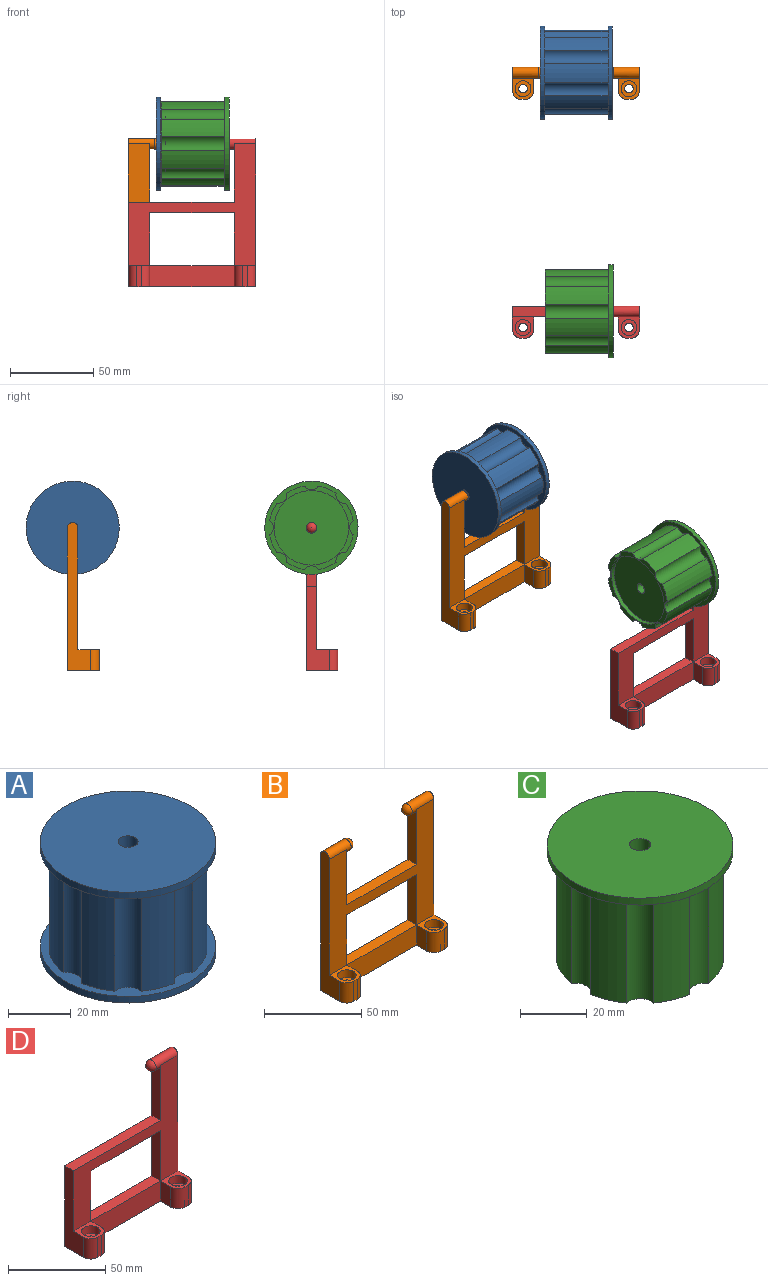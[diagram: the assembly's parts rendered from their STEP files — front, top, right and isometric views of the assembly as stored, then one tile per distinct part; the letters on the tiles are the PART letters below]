
ASSEMBLY  parts=4 mates=4
PART A: 23 faces, bbox 55.9x55.9x43.2 mm
  f0: cylinder r=25.4mm len=38.1mm, axis (0,0,-1), area 440.1mm2, adj f10,f11,f18,f21
  f1: cylinder r=25.4mm len=38.1mm, axis (0,0,-1), area 440.1mm2, adj f10,f17,f18,f21
  f2: cylinder r=25.4mm len=38.1mm, axis (0,0,-1), area 440.1mm2, adj f10,f16,f17,f21
  f3: cylinder r=25.4mm len=38.1mm, axis (0,0,-1), area 440.1mm2, adj f10,f15,f16,f21
  f4: cylinder r=25.4mm len=38.1mm, axis (0,0,-1), area 440.1mm2, adj f10,f14,f15,f21
  f5: cylinder r=25.4mm len=38.1mm, axis (0,0,-1), area 440.1mm2, adj f10,f13,f14,f21
  f6: cylinder r=25.4mm len=38.1mm, axis (0,0,-1), area 440.1mm2, adj f10,f12,f13,f21
  f7: cylinder r=25.4mm len=38.1mm, axis (0,0,-1), area 440.1mm2, adj f10,f11,f12,f21
  f8: cylinder r=27.94mm len=55.88mm, axis (0,0,-1), area 445.9mm2, adj f9,f10
  f9: plane 55.88x55.88mm, normal (0,0,1), area 2420.8mm2, adj f8,f22
  f10: plane 55.88x55.88mm, normal (0,0,-1), area 544.1mm2, adj f0,f1,f2,f3,f4,f5,f6,f7
  f11: cylinder r=5.08mm len=38.1mm, axis (0,0,-1), area 374.1mm2, adj f0,f7,f10,f21
  f12: cylinder r=5.08mm len=38.1mm, axis (0,0,-1), area 374.1mm2, adj f6,f7,f10,f21
  f13: cylinder r=5.08mm len=38.1mm, axis (0,0,-1), area 374.1mm2, adj f5,f6,f10,f21
  f14: cylinder r=5.08mm len=38.1mm, axis (0,0,-1), area 374.1mm2, adj f4,f5,f10,f21
  f15: cylinder r=5.08mm len=38.1mm, axis (0,0,-1), area 374.1mm2, adj f3,f4,f10,f21
  f16: cylinder r=5.08mm len=38.1mm, axis (0,0,-1), area 374.1mm2, adj f2,f3,f10,f21
  f17: cylinder r=5.08mm len=38.1mm, axis (0,0,-1), area 374.1mm2, adj f1,f2,f10,f21
  f18: cylinder r=5.08mm len=38.1mm, axis (0,0,-1), area 374.1mm2, adj f0,f1,f10,f21
  f19: cylinder r=27.94mm len=55.88mm, axis (0,0,1), area 445.9mm2, adj f20,f21
  f20: plane 55.88x55.88mm, normal (0,0,-1), area 2420.8mm2, adj f19,f22
  f21: plane 55.88x55.88mm, normal (0,0,1), area 544.1mm2, adj f0,f1,f2,f3,f4,f5,f6,f7
  f22: cylinder r=3.17mm len=43.18mm, axis (0,0,-1), area 861.4mm2, adj f9,f20
PART B: 33 faces, bbox 76.2x19.1x88.9 mm
  f0: plane 50.8x12.7mm, normal (0,-1,0), area 645.2mm2, adj f3,f16,f17,f20
  f1: plane 76.2x73.03mm, normal (0,-1,0), area 2177.4mm2, adj f4,f5,f6,f7,f8,f9,f10,f13
  f2: plane 85.73x76.2mm, normal (0,1,0), area 3145.2mm2, adj f3,f4,f5,f6,f7,f8,f9,f10
  f3: plane 76.2x19.05mm, normal (0,0,-1), area 743.4mm2, adj f0,f2,f4,f5,f17,f19,f20,f22
  f4: plane 88.9x13.97mm, normal (1,0,0), area 657mm2, adj f1,f2,f3,f10,f21,f29
  f5: plane 88.9x13.97mm, normal (-1,0,0), area 657mm2, adj f1,f2,f3,f9,f18,f32
  f6: plane 34.93x6.35mm, normal (-1,0,0), area 205.9mm2, adj f1,f2,f8,f10
  f7: plane 34.93x6.35mm, normal (1,0,0), area 205.9mm2, adj f1,f2,f8,f9
  f8: plane 50.8x6.35mm, normal (0,0,1), area 322.6mm2, adj f1,f2,f6,f7
  f9: cylinder r=3.17mm len=15.88mm, axis (-1,0,0), area 190mm2, adj f1,f2,f5,f7,f12
  f10: cylinder r=3.17mm len=15.88mm, axis (1,0,0), area 190mm2, adj f1,f2,f4,f6,f11
  f11: sphere r=3.17mm, area 63.3mm2, adj f10
  f12: sphere r=3.17mm, area 63.3mm2, adj f9
  f13: plane 31.75x6.35mm, normal (-1,0,0), area 201.6mm2, adj f1,f2,f14,f16
  f14: plane 50.8x6.35mm, normal (0,0,-1), area 322.6mm2, adj f1,f2,f13,f15
  f15: plane 31.75x6.35mm, normal (1,0,0), area 201.6mm2, adj f1,f2,f14,f16
  f16: plane 50.8x6.35mm, normal (0,0,1), area 322.6mm2, adj f0,f2,f13,f15
  f17: plane 12.7x7.62mm, normal (1,0,0), area 96.8mm2, adj f0,f3,f18,f31
  f18: plane 12.7x12.7mm, normal (0,0,1), area 79mm2, adj f1,f5,f17,f19,f25,f31,f32
  f19: plane 12.7x2.54mm, normal (0,-1,0), area 32.3mm2, adj f3,f18,f31,f32
  f20: plane 12.7x7.62mm, normal (-1,0,0), area 96.8mm2, adj f0,f3,f21,f30
  f21: plane 12.7x12.7mm, normal (0,0,1), area 79mm2, adj f1,f4,f20,f22,f28,f29,f30
  f22: plane 12.7x2.54mm, normal (0,-1,0), area 32.3mm2, adj f3,f21,f29,f30
  f23: cylinder r=2.55mm len=7.87mm, axis (0,0,1), area 126.3mm2, adj f3,f24
  f24: plane 9.53x9.53mm, normal (0,0,1), area 50.8mm2, adj f23,f25
  f25: cylinder r=4.76mm len=9.53mm, axis (0,0,1), area 144.4mm2, adj f18,f24
  f26: cylinder r=2.55mm len=7.87mm, axis (0,0,1), area 126.3mm2, adj f3,f27
  f27: plane 9.53x9.53mm, normal (0,0,1), area 50.8mm2, adj f26,f28
  f28: cylinder r=4.76mm len=9.53mm, axis (0,0,1), area 144.4mm2, adj f21,f27
  f29: cylinder r=5.08mm len=12.7mm, axis (0,0,-1), area 101.3mm2, adj f3,f4,f21,f22
  f30: cylinder r=5.08mm len=12.7mm, axis (0,0,1), area 101.3mm2, adj f3,f20,f21,f22
  f31: cylinder r=5.08mm len=12.7mm, axis (0,0,-1), area 101.3mm2, adj f3,f17,f18,f19
  f32: cylinder r=5.08mm len=12.7mm, axis (0,0,1), area 101.3mm2, adj f3,f5,f18,f19
PART C: 23 faces, bbox 55.9x55.9x40.6 mm
  f0: cylinder r=25.4mm len=38.1mm, axis (0,0,-1), area 440.1mm2, adj f1,f11,f15,f22
  f1: plane 50.11x50.11mm, normal (0,0,-1), area 338.8mm2, adj f0,f2,f3,f4,f5,f6,f7,f8
  f2: cylinder r=25.4mm len=38.1mm, axis (0,0,-1), area 440.1mm2, adj f1,f11,f21,f22
  f3: cylinder r=25.4mm len=38.1mm, axis (0,0,-1), area 440.1mm2, adj f1,f11,f20,f21
  f4: cylinder r=25.4mm len=38.1mm, axis (0,0,-1), area 440.1mm2, adj f1,f11,f19,f20
  f5: cylinder r=25.4mm len=38.1mm, axis (0,0,-1), area 440.1mm2, adj f1,f11,f18,f19
  f6: cylinder r=25.4mm len=38.1mm, axis (0,0,-1), area 440.1mm2, adj f1,f11,f17,f18
  f7: cylinder r=25.4mm len=38.1mm, axis (0,0,-1), area 440.1mm2, adj f1,f11,f16,f17
  f8: cylinder r=25.4mm len=38.1mm, axis (0,0,-1), area 440.1mm2, adj f1,f11,f15,f16
  f9: cylinder r=27.94mm len=55.88mm, axis (0,0,-1), area 445.9mm2, adj f10,f11
  f10: plane 55.88x55.88mm, normal (0,0,1), area 2420.8mm2, adj f9,f14
  f11: plane 55.88x55.88mm, normal (0,0,-1), area 544.1mm2, adj f0,f2,f3,f4,f5,f6,f7,f8
  f12: cylinder r=22.35mm len=44.7mm, axis (0,0,-1), area 356.7mm2, adj f1,f13
  f13: plane 44.7x44.7mm, normal (0,0,-1), area 1537.9mm2, adj f12,f14
  f14: cylinder r=3.17mm len=38.1mm, axis (0,0,-1), area 760.1mm2, adj f10,f13
  f15: cylinder r=5.08mm len=38.1mm, axis (0,0,-1), area 374.1mm2, adj f0,f1,f8,f11
  f16: cylinder r=5.08mm len=38.1mm, axis (0,0,-1), area 374.1mm2, adj f1,f7,f8,f11
  f17: cylinder r=5.08mm len=38.1mm, axis (0,0,-1), area 374.1mm2, adj f1,f6,f7,f11
  f18: cylinder r=5.08mm len=38.1mm, axis (0,0,-1), area 374.1mm2, adj f1,f5,f6,f11
  f19: cylinder r=5.08mm len=38.1mm, axis (0,0,-1), area 374.1mm2, adj f1,f4,f5,f11
  f20: cylinder r=5.08mm len=38.1mm, axis (0,0,-1), area 374.1mm2, adj f1,f3,f4,f11
  f21: cylinder r=5.08mm len=38.1mm, axis (0,0,-1), area 374.1mm2, adj f1,f2,f3,f11
  f22: cylinder r=5.08mm len=38.1mm, axis (0,0,-1), area 374.1mm2, adj f0,f1,f2,f11
PART D: 30 faces, bbox 76.2x19.1x88.9 mm
  f0: plane 50.8x12.7mm, normal (0,-1,0), area 645.2mm2, adj f3,f13,f14,f17
  f1: plane 76.2x73.03mm, normal (0,-1,0), area 1733.9mm2, adj f4,f5,f6,f7,f8,f10,f11,f12
  f2: plane 85.73x76.2mm, normal (0,1,0), area 2701.6mm2, adj f3,f4,f5,f6,f7,f8,f10,f11
  f3: plane 76.2x19.05mm, normal (0,0,-1), area 743.4mm2, adj f0,f2,f4,f5,f14,f16,f17,f19
  f4: plane 88.9x13.97mm, normal (1,0,0), area 657mm2, adj f1,f2,f3,f8,f18,f26
  f5: plane 50.8x13.97mm, normal (-1,0,0), area 419.4mm2, adj f1,f2,f3,f7,f15,f29
  f6: plane 34.93x6.35mm, normal (-1,0,0), area 205.9mm2, adj f1,f2,f7,f8
  f7: plane 63.5x6.35mm, normal (0,0,1), area 403.2mm2, adj f1,f2,f5,f6
  f8: cylinder r=3.17mm len=15.88mm, axis (1,0,0), area 190mm2, adj f1,f2,f4,f6,f9
  f9: sphere r=3.17mm, area 63.3mm2, adj f8
  f10: plane 31.75x6.35mm, normal (-1,0,0), area 201.6mm2, adj f1,f2,f11,f13
  f11: plane 50.8x6.35mm, normal (0,0,-1), area 322.6mm2, adj f1,f2,f10,f12
  f12: plane 31.75x6.35mm, normal (1,0,0), area 201.6mm2, adj f1,f2,f11,f13
  f13: plane 50.8x6.35mm, normal (0,0,1), area 322.6mm2, adj f0,f2,f10,f12
  f14: plane 12.7x7.62mm, normal (1,0,0), area 96.8mm2, adj f0,f3,f15,f28
  f15: plane 12.7x12.7mm, normal (0,0,1), area 79mm2, adj f1,f5,f14,f16,f22,f28,f29
  f16: plane 12.7x2.54mm, normal (0,-1,0), area 32.3mm2, adj f3,f15,f28,f29
  f17: plane 12.7x7.62mm, normal (-1,0,0), area 96.8mm2, adj f0,f3,f18,f27
  f18: plane 12.7x12.7mm, normal (0,0,1), area 79mm2, adj f1,f4,f17,f19,f25,f26,f27
  f19: plane 12.7x2.54mm, normal (0,-1,0), area 32.3mm2, adj f3,f18,f26,f27
  f20: cylinder r=2.55mm len=7.87mm, axis (0,0,1), area 126.3mm2, adj f3,f21
  f21: plane 9.53x9.53mm, normal (0,0,1), area 50.8mm2, adj f20,f22
  f22: cylinder r=4.76mm len=9.53mm, axis (0,0,1), area 144.4mm2, adj f15,f21
  f23: cylinder r=2.55mm len=7.87mm, axis (0,0,1), area 126.3mm2, adj f3,f24
  f24: plane 9.53x9.53mm, normal (0,0,1), area 50.8mm2, adj f23,f25
  f25: cylinder r=4.76mm len=9.53mm, axis (0,0,1), area 144.4mm2, adj f18,f24
  f26: cylinder r=5.08mm len=12.7mm, axis (0,0,-1), area 101.3mm2, adj f3,f4,f18,f19
  f27: cylinder r=5.08mm len=12.7mm, axis (0,0,1), area 101.3mm2, adj f3,f17,f18,f19
  f28: cylinder r=5.08mm len=12.7mm, axis (0,0,-1), area 101.3mm2, adj f3,f14,f15,f16
  f29: cylinder r=5.08mm len=12.7mm, axis (0,0,1), area 101.3mm2, adj f3,f5,f15,f16
PLACE A rot(axis=(0.49,0.72,0.49),108.5deg) t=(0.17,-3.18,41.28)mm
PLACE B at identity fixed
PLACE C rot(axis=(0,1,0),90deg) t=(0.64,-146.35,41.28)mm
PLACE D t=(0,-143.18,0)mm
MATE cylindrical C.f9 <-> D.f8  axis (1,0,0) through (22.22,-146.35,41.28)mm
MATE planar D.f3 <-> B.f3  axis (0,0,-1) through (0,-149.52,-44.45)mm
MATE planar B.f4 <-> D.f4  axis (1,0,0) through (38.1,-4.2,-5.9)mm
MATE cylindrical B.f10 <-> A.f8  axis (1,0,0) through (22.22,-3.18,41.28)mm
